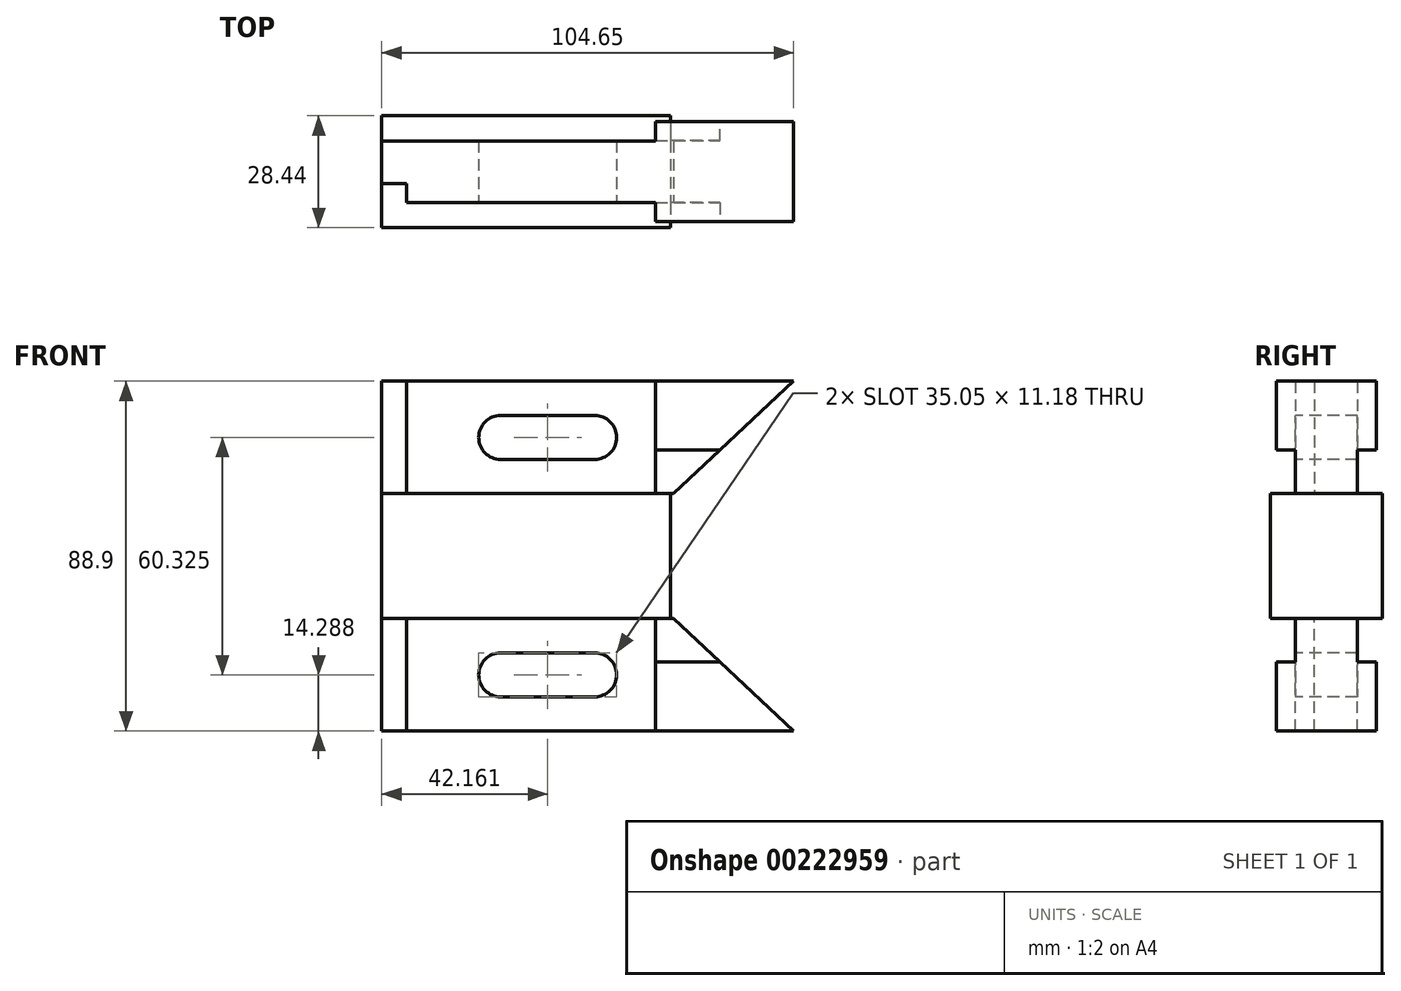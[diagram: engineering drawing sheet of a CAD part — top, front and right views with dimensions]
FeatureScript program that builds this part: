
annotation { "Feature Type Name" : "Feature", "Feature Type Description" : "" }
export const myFeature = defineFeature(function(context is Context, id is Id, definition is map)
    precondition{}
    {
        {
            var Q0;
            Q0=qCreatedBy(makeId("Front.planeOp"),FACE);
            var sketch = newSketch(context, id + "F0", { "sketchPlane" : qUnion([Q0])});
            skLineSegment(sketch, "E0.bottom", {"start": v(36.7, -15.88) * mm, "end": v(-36.7, -15.88) * mm});
            skLineSegment(sketch, "E0.top", {"start": v(36.7, 15.88) * mm, "end": v(-36.7, 15.88) * mm});
            skLineSegment(sketch, "E0.left", {"start": v(36.7, -15.88) * mm, "end": v(36.7, 15.88) * mm});
            skLineSegment(sketch, "E0.right", {"start": v(-36.7, -15.88) * mm, "end": v(-36.7, 15.88) * mm});
            skPoint(sketch, "E0.middle", {"position": v(0, 0) * mm});
            skSolve(sketch);
        }
        {
            var Q0;
            Q0 = qSketchRegion(id + "F0", true);
            extrude(context, id + "F1", {"entities" : qUnion([Q0]), "endBound" : BoundingType.SYMMETRIC, "oppositeDirection" : true, "depth" : 28.45 * mm});
        }
        {
            var Q0;
            Q0=makeQuery(id+"F1.opExtrude","SWEPT_FACE",FACE,{"disambiguationData":[OSD([sQuery(id+"F0.wireOp",EDGE,"E0.top")])]});
            var sketch = newSketch(context, id + "F2", { "sketchPlane" : qUnion([Q0])});
            skLineSegment(sketch, "E1", {"start": v(-36.7, -3.05) * mm, "end": v(-30.35, -3.05) * mm});
            skLineSegment(sketch, "E2", {"start": v(-30.35, -3.05) * mm, "end": v(-30.35, -7.85) * mm});
            skLineSegment(sketch, "E3", {"start": v(-36.7, 7.85) * mm, "end": v(32.9, 7.85) * mm});
            skLineSegment(sketch, "E4", {"start": v(-30.35, -7.85) * mm, "end": v(32.9, -7.85) * mm});
            skLineSegment(sketch, "E5", {"start": v(-36.7, -3.05) * mm, "end": v(-36.7, 7.85) * mm});
            skLineSegment(sketch, "E6", {"start": v(32.9, 7.85) * mm, "end": v(32.9, 12.7) * mm});
            skLineSegment(sketch, "E7", {"start": v(32.9, -7.85) * mm, "end": v(32.9, -12.7) * mm});
            skLineSegment(sketch, "E8", {"start": v(32.9, 12.7) * mm, "end": v(67.95, 12.7) * mm});
            skLineSegment(sketch, "E9", {"start": v(32.9, -12.7) * mm, "end": v(67.95, -12.7) * mm});
            skLineSegment(sketch, "E10", {"start": v(67.95, -12.7) * mm, "end": v(67.95, 12.7) * mm});
            skSolve(sketch);
        }
        {
            var Q0;
            Q0 = qSketchRegion(id + "F2", true);
            extrude(context, id + "F3", {"entities" : qUnion([Q0]), "operationType" : NewBodyOperationType.ADD, "depth" : 28.57 * mm});
        }
        {
            var Q0;
            Q0=makeQuery(id+"F3.opExtrude","SWEPT_FACE",FACE,{"disambiguationData":[OSD([sQuery(id+"F2.wireOp",EDGE,"E9")])]});
            var sketch = newSketch(context, id + "F4", { "sketchPlane" : qUnion([Q0])});
            skLineSegment(sketch, "E11", {"start": v(37.47, 15.88) * mm, "end": v(67.95, 44.45) * mm});
            skLineSegment(sketch, "E12", {"start": v(37.47, 15.88) * mm, "end": v(67.95, 15.88) * mm});
            skLineSegment(sketch, "E13", {"start": v(67.95, 15.88) * mm, "end": v(67.95, 44.45) * mm});
            skSolve(sketch);
        }
        {
            var Q0;
            Q0=makeQuery(id+"F4.imprint","IMPRINT",FACE,{"disambiguationData":[TD([[makeQuery(id+"F4.imprint","IMPRINT",EDGE,{"derivedFrom":sQuery(id+"F4.wireOp",EDGE,"E11")}),-1.0]])]});
            extrude(context, id + "F5", {"entities" : qUnion([Q0]), "operationType" : NewBodyOperationType.REMOVE, "oppositeDirection" : true, "depth" : 25.4 * mm});
        }
        {
            var Q0;
            Q0=makeQuery(id+"F1.opExtrude","SWEPT_BODY",BODY,{"disambiguationData":[OSD([sQuery(id+"F0.wireOp",EDGE,"E0.bottom"),sQuery(id+"F0.wireOp",EDGE,"E0.top"),sQuery(id+"F0.wireOp",EDGE,"E0.left"),sQuery(id+"F0.wireOp",EDGE,"E0.right")])]});
            var Q1;
            Q1=qCreatedBy(makeId("Top.planeOp"),FACE);
            mirror(context, id + "F6", {"operationType" : NewBodyOperationType.ADD, "entities" : qUnion([Q0]), "mirrorPlane" : qUnion([Q1])});
        }
        {
            var Q0;
            Q0=qCreatedBy(makeId("Front.planeOp"),FACE);
            var sketch = newSketch(context, id + "F7", { "sketchPlane" : qUnion([Q0])});
            skLineSegment(sketch, "E14", {"start": v(-36.7, -30.16) * mm, "end": v(-12.07, -30.16) * mm});
            skLineSegment(sketch, "E15", {"start": v(-12.07, -30.16) * mm, "end": v(22.99, -30.16) * mm});
            skArc(sketch, "E16", {"start": v(-6.48, -24.57) * mm, "mid": v(-12.07, -30.16) * mm, "end": v(-6.48, -35.75) * mm});
            skArc(sketch, "E17.MirrorCS", {"start": v(17.4, -24.57) * mm, "mid": v(22.99, -30.16) * mm, "end": v(17.4, -35.75) * mm});
            skLineSegment(sketch, "E18", {"start": v(-6.48, -24.57) * mm, "end": v(17.4, -24.57) * mm});
            skLineSegment(sketch, "E19", {"start": v(-6.48, -35.75) * mm, "end": v(17.4, -35.75) * mm});
            skLineSegment(sketch, "E20.MirrorCS", {"start": v(-6.48, 24.57) * mm, "end": v(17.4, 24.57) * mm});
            skArc(sketch, "E21.MirrorCS", {"start": v(-6.48, 24.57) * mm, "mid": v(-12.07, 30.16) * mm, "end": v(-6.48, 35.75) * mm});
            skArc(sketch, "E22.MirrorCS", {"start": v(17.4, 24.57) * mm, "mid": v(22.99, 30.16) * mm, "end": v(17.4, 35.75) * mm});
            skLineSegment(sketch, "E23.MirrorCS", {"start": v(-6.48, 35.75) * mm, "end": v(17.4, 35.75) * mm});
            skSolve(sketch);
        }
        {
            var Q0;
            Q0 = qSketchRegion(id + "F7", true);
            extrude(context, id + "F8", {"entities" : qUnion([Q0]), "operationType" : NewBodyOperationType.REMOVE, "endBound" : BoundingType.SYMMETRIC, "oppositeDirection" : true, "depth" : 25.4 * mm});
        }
        {
            var Q0;
            Q0=makeQuery(id+"F6.opPattern","COPY",FACE,{"derivedFrom":makeQuery(id+"F3.opExtrude","SWEPT_FACE",FACE,{"disambiguationData":[OSD([sQuery(id+"F2.wireOp",EDGE,"E9")])]}),"instanceName":"1"});
            var sketch = newSketch(context, id + "F9", { "sketchPlane" : qUnion([Q0])});
            skLineSegment(sketch, "E24", {"start": v(32.9, -44.45) * mm, "end": v(32.9, -26.92) * mm});
            skLineSegment(sketch, "E25", {"start": v(32.9, -26.92) * mm, "end": v(49.25, -26.92) * mm});
            skLineSegment(sketch, "E26", {"start": v(49.25, -26.92) * mm, "end": v(37.47, -15.88) * mm});
            skLineSegment(sketch, "E27", {"start": v(37.47, -15.88) * mm, "end": v(32.9, -15.88) * mm});
            skLineSegment(sketch, "E28", {"start": v(32.9, -15.88) * mm, "end": v(32.9, -26.92) * mm});
            skLineSegment(sketch, "E29.MirrorCS", {"start": v(49.25, 26.92) * mm, "end": v(37.47, 15.88) * mm});
            skLineSegment(sketch, "E30.MirrorCS", {"start": v(37.47, 15.88) * mm, "end": v(32.9, 15.88) * mm});
            skLineSegment(sketch, "E31.MirrorCS", {"start": v(32.9, 15.88) * mm, "end": v(32.9, 26.92) * mm});
            skLineSegment(sketch, "E32.MirrorCS", {"start": v(32.9, 26.92) * mm, "end": v(49.25, 26.92) * mm});
            skSolve(sketch);
        }
        {
            var Q0;
            Q0 = qSketchRegion(id + "F9", true);
            extrude(context, id + "F10", {"entities" : qUnion([Q0]), "operationType" : NewBodyOperationType.REMOVE, "oppositeDirection" : true, "depth" : 4.83 * mm});
        }
        {
            var Q0;
            Q0=makeQuery(id+"F6.opPattern","COPY",FACE,{"derivedFrom":makeQuery(id+"F3.opExtrude","SWEPT_FACE",FACE,{"disambiguationData":[OSD([sQuery(id+"F2.wireOp",EDGE,"E8")])]}),"instanceName":"1"});
            var sketch = newSketch(context, id + "F11", { "sketchPlane" : qUnion([Q0])});
            skLineSegment(sketch, "E33", {"start": v(-32.9, -44.45) * mm, "end": v(-32.9, -26.92) * mm});
            skLineSegment(sketch, "E34", {"start": v(-32.9, -26.92) * mm, "end": v(-49.25, -26.92) * mm});
            skLineSegment(sketch, "E35", {"start": v(-36.7, -15.88) * mm, "end": v(-32.9, -15.88) * mm});
            skLineSegment(sketch, "E36", {"start": v(-32.9, -15.88) * mm, "end": v(-32.9, -26.92) * mm});
            skLineSegment(sketch, "E37.MirrorCS", {"start": v(-36.7, 15.88) * mm, "end": v(-32.9, 15.88) * mm});
            skLineSegment(sketch, "E38", {"start": v(-49.25, -26.92) * mm, "end": v(-37.47, -15.88) * mm});
            skLineSegment(sketch, "E39", {"start": v(-37.47, -15.88) * mm, "end": v(-36.7, -15.88) * mm});
            skLineSegment(sketch, "E40.MirrorCS", {"start": v(-49.25, 26.92) * mm, "end": v(-37.47, 15.88) * mm});
            skLineSegment(sketch, "E41.MirrorCS", {"start": v(-37.47, 15.88) * mm, "end": v(-36.7, 15.88) * mm});
            skLineSegment(sketch, "E42.MirrorCS", {"start": v(-32.9, 15.88) * mm, "end": v(-32.9, 26.92) * mm});
            skLineSegment(sketch, "E43.MirrorCS", {"start": v(-32.9, 26.92) * mm, "end": v(-49.25, 26.92) * mm});
            skSolve(sketch);
        }
        {
            var Q0;
            Q0 = qSketchRegion(id + "F11", true);
            extrude(context, id + "F12", {"entities" : qUnion([Q0]), "operationType" : NewBodyOperationType.REMOVE, "oppositeDirection" : true, "depth" : 4.83 * mm});
        }
    });
